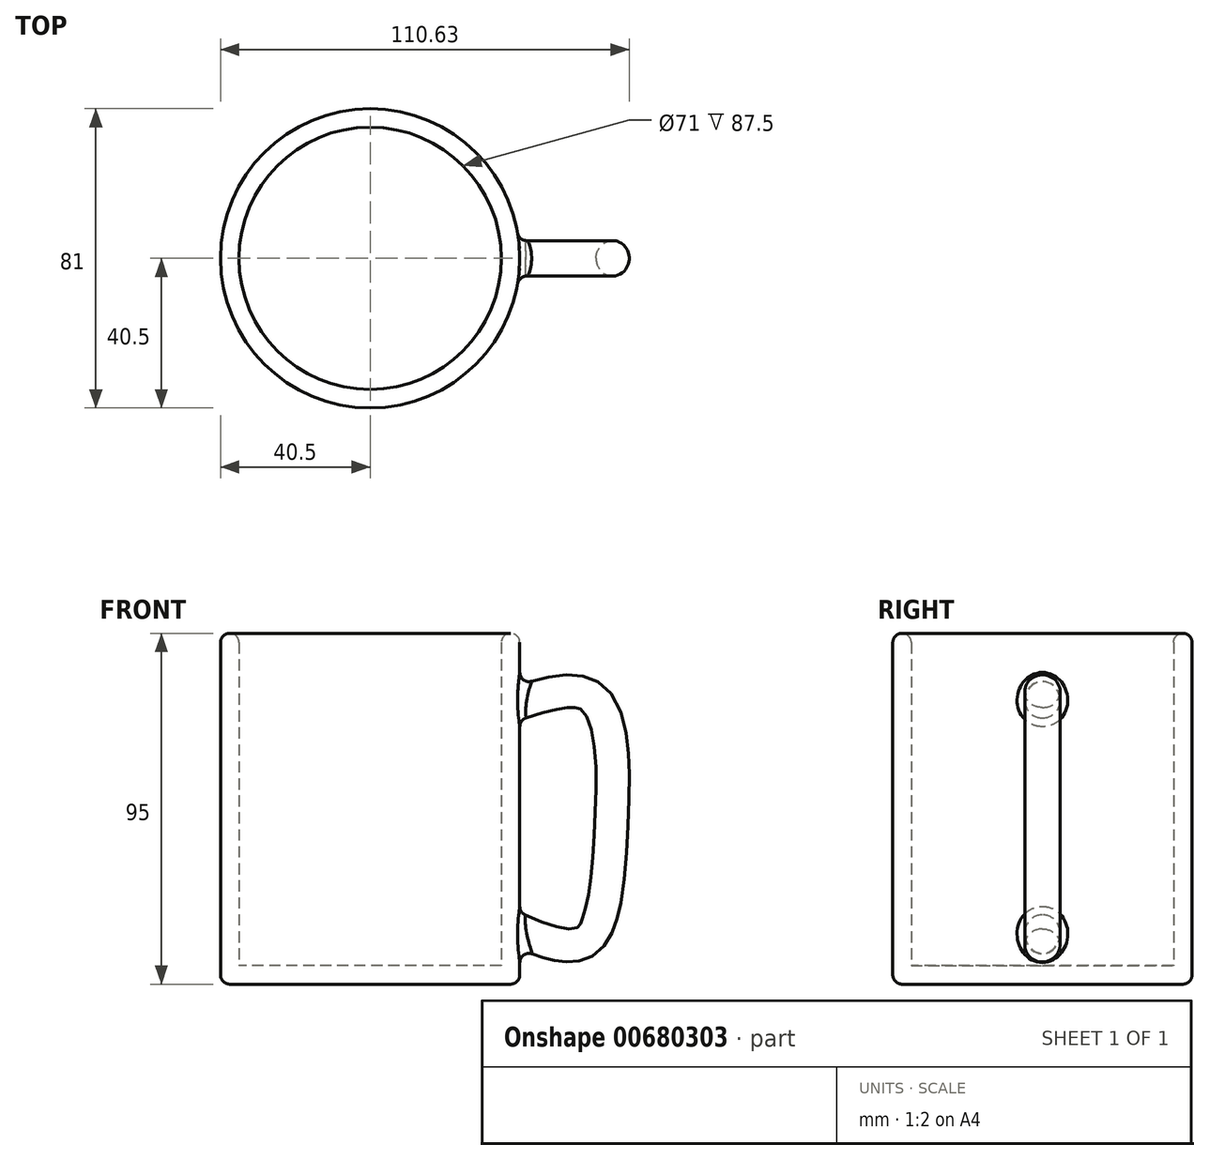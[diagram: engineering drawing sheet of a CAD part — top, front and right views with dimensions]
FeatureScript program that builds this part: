
annotation { "Feature Type Name" : "Feature", "Feature Type Description" : "" }
export const myFeature = defineFeature(function(context is Context, id is Id, definition is map)
    precondition{}
    {
        {
            var Q0;
            Q0=qCreatedBy(makeId("Top.planeOp"),FACE);
            var sketch = newSketch(context, id + "F0", { "sketchPlane" : qUnion([Q0])});
            skCircle(sketch, "E0", {"center": v(0, 0) * mm, "radius": 40.5 * mm});
            skSolve(sketch);
        }
        {
            var Q0;
            Q0 = qSketchRegion(id + "F0", true);
            extrude(context, id + "F1", {"entities" : qUnion([Q0]), "depth" : 95 * mm, "offsetDistance" : 25 * mm});
        }
        {
            var Q0;
            Q0=qCreatedBy(makeId("Front.planeOp"),FACE);
            var sketch = newSketch(context, id + "F2", { "sketchPlane" : qUnion([Q0])});
            skFitSpline(sketch, "E1", {"points": [v(34.36, 74.16) * mm, v(60.22, 77.45) * mm, v(65.29, 41.04) * mm, v(57.71, 11.42) * mm, v(34.44, 17.23) * mm], "startDerivative": vector(130.05, 47.8) * mm, "endDerivative": vector(-119.56, 57.85) * mm});
            skSolve(sketch);
        }
        {
            var Q0;
            Q0=qCreatedBy(makeId("Right.planeOp"),FACE);
            cPlane(context, id + "F3", {"entities" : qUnion([Q0]), "cplaneType" : CPlaneType.OFFSET, "offset" : 35.1 * mm, "width" : 150 * mm, "height" : 150 * mm});
        }
        {
            var Q0;
            Q0=qCreatedBy(id+"F3.planeOp",FACE);
            var sketch = newSketch(context, id + "F4", { "sketchPlane" : qUnion([Q0])});
            skCircle(sketch, "E2", {"center": v(0, 74.3) * mm, "radius": 4.8 * mm});
            skSolve(sketch);
        }
        {
            var Q0;
            Q0 = qSketchRegion(id + "F4", true);
            var Q1;
            Q1 = qConstructionFilter(qBodyType(qCreatedBy(id + "F2" ,EDGE), BodyType.WIRE), ConstructionObject.NO);
            sweep(context, id + "F5", {"operationType" : NewBodyOperationType.ADD, "profiles" : qUnion([Q0]), "path" : qUnion([Q1])});
        }
        {
            var Q0;
            Q0=makeQuery(id+"F1.opExtrude","CAP_FACE",FACE,{"disambiguationData":[OSD([sQuery(id+"F0.wireOp",EDGE,"E0")])],"isStart":false});
            shell(context, id + "F6", {"entities" : qUnion([Q0]), "thickness" : 5 * mm});
        }
        {
            var Q0;
            {var subQ0=sQuery(id+"F0.wireOp",EDGE,"E0");Q0=makeQuery(id+"F6.opShell","OFFSET_EDGE",EDGE,{"disambiguationData":[OSD([subQ0]),TDD([makeQuery(id+"F1.opExtrude","CAP_EDGE",EDGE,{"disambiguationData":[OSD([subQ0])],"isStart":false})])]});}
            var Q1;
            Q1=makeQuery(id+"F1.opExtrude","CAP_EDGE",EDGE,{"disambiguationData":[OSD([sQuery(id+"F0.wireOp",EDGE,"E0")])],"isStart":false});
            var Q2;
            Q2=makeQuery(id+"F5.boolean.opBoolean","INTERSECT",EDGE,{"disambiguationData":[OD(1.0)],"derivedFrom":[makeQuery(id+"F1.opExtrude","SWEPT_FACE",FACE,{"disambiguationData":[OSD([sQuery(id+"F0.wireOp",EDGE,"E0")])]}),makeQuery(id+"F5.opSweep","SWEPT_FACE",FACE,{"disambiguationData":[OSD([sQuery(id+"F2.wireOp",EDGE,"E1"),sQuery(id+"F4.wireOp",EDGE,"E2")])]})]});
            var Q3;
            Q3=makeQuery(id+"F5.boolean.opBoolean","INTERSECT",EDGE,{"disambiguationData":[OD(0.0)],"derivedFrom":[makeQuery(id+"F1.opExtrude","SWEPT_FACE",FACE,{"disambiguationData":[OSD([sQuery(id+"F0.wireOp",EDGE,"E0")])]}),makeQuery(id+"F5.opSweep","SWEPT_FACE",FACE,{"disambiguationData":[OSD([sQuery(id+"F2.wireOp",EDGE,"E1"),sQuery(id+"F4.wireOp",EDGE,"E2")])]})]});
            var Q4;
            Q4=makeQuery(id+"F1.opExtrude","CAP_EDGE",EDGE,{"disambiguationData":[OSD([sQuery(id+"F0.wireOp",EDGE,"E0")])],"isStart":true});
            fillet(context, id + "F7", {"entities" : qUnion([Q0, Q1, Q2, Q3, Q4]), "radius" : 2.5 * mm, "tangentPropagation" : true, "allowEdgeOverflow" : false});
        }
    });
